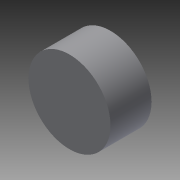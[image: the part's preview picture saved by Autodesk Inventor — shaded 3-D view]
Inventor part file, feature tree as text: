
AUTODESK INVENTOR PART (.ipt)
format: ipt  version: 2014 (Build 180170000, 170)  size: 71,168 bytes
history: native  units: mm
features: extrude x1, sketch x1
ambient origin geometry x8: Origin, YZ Plane, XZ Plane, XY Plane, X Axis, Y Axis, Z Axis, Center Point
bodies: Volumenkörper1 (feature_tree)
feature tree (2):
  extrude  "Extrusion1"  Depth=50.0mm TaperAngle=0.0deg
  sketch  "Skizze1"  dims[d0=100.0mm d1=50.0mm d2=0.0mm]
